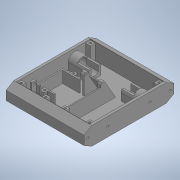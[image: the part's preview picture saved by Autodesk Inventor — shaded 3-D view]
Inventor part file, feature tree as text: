
AUTODESK INVENTOR PART (.ipt)
format: ipt  version: 2020 (Build 240168000, 168)  size: 648,192 bytes
history: native  units: in
note: dims shown in document units (in); Inventor stores cm internally (conversion verified against a paired STEP export)
features: extrude x19, sketch x19, projected_geometry x14, mirror x6, plane x1
ambient origin geometry x8: Origin, YZ Plane, XZ Plane, XY Plane, X Axis, Y Axis, Z Axis, Center Point
bodies: Solid1 (feature_tree)
feature tree (59):
  extrude  "Extrusion1"  Depth=5.9055in
  extrude  "Extrusion2"  TaperAngle=0.0deg  [1 undecoded]
  extrude  "Extrusion3"  Depth=1.063in
  extrude  "Extrusion4"  Depth=0.315in
  extrude  "Extrusion5"  TaperAngle=0.0deg  [1 undecoded]
  extrude  "Extrusion6"  Depth=0.5906in
  mirror  "Mirror1"
  extrude  "Extrusion7"  Depth=0.0787in
  mirror  "Mirror2"
  extrude  "Extrusion8"  Depth=0.6102in
  mirror  "Mirror3"
  plane  "Work Plane1"
  extrude  "Extrusion9"  Depth=0.7874in TaperAngle=0.0deg
  mirror  "Mirror4"
  extrude  "Extrusion10"  Depth=6.063in TaperAngle=0.0deg
  extrude  "Extrusion11"  Depth=0.1575in
  extrude  "Extrusion12"  TaperAngle=0.0deg  [1 undecoded]
  extrude  "Extrusion13"  Depth=0.2756in
  extrude  "Extrusion14"  Depth=0.4331in
  extrude  "Extrusion17"  Depth=2.7559in
  extrude  "Extrusion18"  Depth=0.0492in
  mirror  "Mirror6"
  extrude  "Extrusion19"  TaperAngle=0.0deg  [1 undecoded]
  mirror  "Mirror7"
  extrude  "Extrusion20"  Depth=0.0787in
  extrude  "Extrusion21"  Depth=0.993in
  sketch  "Sketch1"  dims[d0=1.1811in d1=5.9055in]
  sketch  "Sketch2"  dims[d2=5.1181in d3=0.0in]
  projected_geometry  "Projected Loop1"
  sketch  "Sketch3"  dims[d4=0.1575in d5=1.063in]
  projected_geometry  "Projected Loop2"
  projected_geometry  "Projected Loop3"
  sketch  "Sketch4"  dims[d6=0.0in d8=0.315in]
  sketch  "Sketch5"  dims[d10=0.993in d11=0.0in]
  projected_geometry  "Projected Loop4"
  sketch  "Sketch6"  dims[d12=0.6496in d13=0.5906in]
  sketch  "Sketch7"  dims[d14=1.5748in d15=0.0787in]
  sketch  "Sketch9"  dims[d16=0.5512in d17=0.0in d18=0.6102in]
  sketch  "Sketch10"  dims[d19=0.4803in d20=0.7874in d21=0.0in]
  sketch  "Sketch12"  dims[d22=0.1654in d23=6.063in d24=0.0in]
  projected_geometry  "Projected Loop6"
  projected_geometry  "Projected Loop7"
  projected_geometry  "Projected Loop8"
  sketch  "Sketch13"  dims[d25=0.5114in d26=0.1575in]
  sketch  "Sketch14"  dims[d27=1.5748in d28=0.0in d29=0.0in]
  sketch  "Sketch15"  dims[d30=0.1575in d31=0.2756in]
  projected_geometry  "Projected Loop15"
  sketch  "Sketch16"  dims[d32=0.0in d33=0.4331in]
  projected_geometry  "Projected Loop19"
  projected_geometry  "Projected Loop20"
  projected_geometry  "Projected Loop21"
  projected_geometry  "Projected Loop22"
  projected_geometry  "Projected Loop23"
  projected_geometry  "Projected Loop24"
  sketch  "Sketch20"  dims[d34=0.0984in d38=2.7559in]
  sketch  "Sketch21"  dims[d40=0.0492in d41=0.0909in]
  sketch  "Sketch22"  dims[d42=0.2362in d43=0.0in]
  sketch  "Sketch23"  dims[d44=60.0deg d45=0.0787in]
  sketch  "Sketch25"  dims[d46=0.315in d48=0.993in d49=0.0in d53=0.2756in d54=0.0in d55=0.4724in d56=1.1811in d57=1.5748in d58=1.5748in d59=0.0787in d60=0.0787in d62=0.315in d63=0.7677in d64=0.0in d66=0.1476in d67=0.2756in d68=0.0in d69=0.7874in d70=0.2953in d71=0.1181in d72=0.0in d89=0.0157in d90=0.0157in d91=0.1476in d92=0.1476in d96=0.315in d97=0.1575in d98=0.1181in d99=0.0in d102=0.1772in d104=0.3346in d105=135.0deg d106=0.2362in d107=0.0in d108=0.0394in d109=0.0in d110=0.063in d111=0.0394in d112=0.0in d117=0.993in d118=0.063in d119=0.3937in d120=0.0in]
note: 4 required parameter values undecoded (feature->parameter linkage not recoverable at this tier; creation-order binding heuristic only, values carry confidence <= 0.55)
